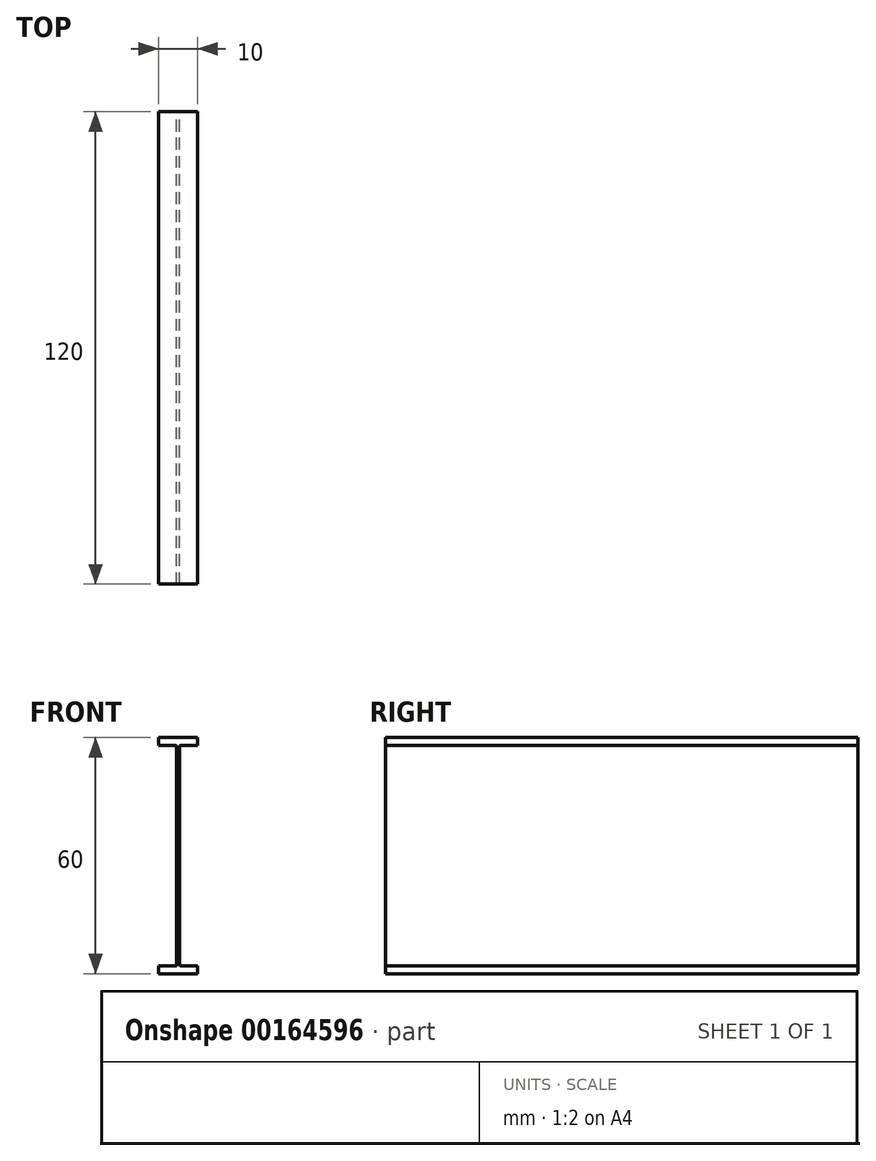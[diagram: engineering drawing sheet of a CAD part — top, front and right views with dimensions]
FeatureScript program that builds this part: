
annotation { "Feature Type Name" : "Feature", "Feature Type Description" : "" }
export const myFeature = defineFeature(function(context is Context, id is Id, definition is map)
    precondition{}
    {
        {
            var Q0;
            Q0=qCreatedBy(makeId("Front.planeOp"),FACE);
            var sketch = newSketch(context, id + "F0", { "sketchPlane" : qUnion([Q0])});
            skLineSegment(sketch, "E0", {"start": v(-4.65, 265) * mm, "end": v(5.35, 265) * mm});
            skLineSegment(sketch, "E1", {"start": v(5.35, 265) * mm, "end": v(5.35, 263) * mm});
            skLineSegment(sketch, "E2", {"start": v(5.35, 263) * mm, "end": v(0.95, 263) * mm});
            skLineSegment(sketch, "E3", {"start": v(0.7, 262.76) * mm, "end": v(0.7, 207.24) * mm});
            skLineSegment(sketch, "E4", {"start": v(0.95, 207) * mm, "end": v(5.35, 207) * mm});
            skLineSegment(sketch, "E5", {"start": v(5.35, 207) * mm, "end": v(5.35, 205) * mm});
            skLineSegment(sketch, "E6", {"start": v(5.35, 205) * mm, "end": v(-4.65, 205) * mm});
            skLineSegment(sketch, "E7", {"start": v(-4.65, 205) * mm, "end": v(-4.65, 207) * mm});
            skLineSegment(sketch, "E8", {"start": v(-4.65, 207) * mm, "end": v(-0.24, 207) * mm});
            skLineSegment(sketch, "E9", {"start": v(0, 207.24) * mm, "end": v(0, 262.76) * mm});
            skLineSegment(sketch, "E10", {"start": v(-0.24, 263) * mm, "end": v(-4.65, 263) * mm});
            skLineSegment(sketch, "E11", {"start": v(-4.65, 263) * mm, "end": v(-4.65, 265) * mm});
            skPoint(sketch, "E12.visualSharp", {"position": v(0.7, 263) * mm});
            skArc(sketch, "E12.filletArc", {"start": v(0.95, 263) * mm, "mid": v(0.78, 262.93) * mm, "end": v(0.7, 262.76) * mm});
            skPoint(sketch, "E13.visualSharp", {"position": v(0, 263) * mm});
            skArc(sketch, "E13.filletArc", {"start": v(0, 262.76) * mm, "mid": v(-0.07, 262.93) * mm, "end": v(-0.24, 263) * mm});
            skPoint(sketch, "E14.visualSharp", {"position": v(0.7, 207) * mm});
            skArc(sketch, "E14.filletArc", {"start": v(0.7, 207.24) * mm, "mid": v(0.78, 207.07) * mm, "end": v(0.95, 207) * mm});
            skPoint(sketch, "E15.visualSharp", {"position": v(0, 207) * mm});
            skArc(sketch, "E15.filletArc", {"start": v(-0.24, 207) * mm, "mid": v(-0.07, 207.07) * mm, "end": v(0, 207.24) * mm});
            skPoint(sketch, "E16", {"position": v(0.35, 265) * mm});
            skPoint(sketch, "E17", {"position": v(0.35, 205) * mm});
            skLineSegment(sketch, "E18", {"start": v(0.35, 265) * mm, "end": v(0.35, 205) * mm, "construction": true});
            skLineSegment(sketch, "E19", {"start": v(0.35, 235) * mm, "end": v(0.7, 235) * mm, "construction": true});
            skLineSegment(sketch, "E20", {"start": v(0.7, 235) * mm, "end": v(0.35, 235) * mm, "construction": true});
            skLineSegment(sketch, "E21", {"start": v(0, 235) * mm, "end": v(0.35, 235) * mm, "construction": true});
            skSolve(sketch);
        }
        {
            var Q0;
            Q0 = qSketchRegion(id + "F0", true);
            extrude(context, id + "F1", {"entities" : qUnion([Q0]), "depth" : 120 * mm});
        }
    });
